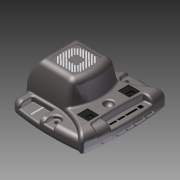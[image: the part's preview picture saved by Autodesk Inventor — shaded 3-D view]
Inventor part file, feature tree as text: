
AUTODESK INVENTOR PART (.ipt)
format: ipt  version: 2014 (Build 180170000, 170)  size: 2,946,560 bytes
history: native  units: mm
features: extrude x8, sketch x6, mirror x3, plane x2, imported_body x1, other x1
ambient origin geometry x8: Origin, YZ Plane, XZ Plane, XY Plane, X Axis, Y Axis, Z Axis, Center Point
bodies: Solid1 (feature_tree)
feature tree (21):
  imported_body  "Base1"
  sketch  "Sketch1"  dims[d50=0.9144mm d57=1.467403mm]
  extrude  "Extrusion2"  Depth=1.467403mm
  plane  "Work Plane1"
  mirror  "Mirror1"
  extrude  "Extrusion3"  Depth=1.467403mm
  sketch  "Sketch2"  dims[d58=1.467403mm d59=1.467403mm]
  extrude  "Extrusion4"  Depth=1.467403mm
  extrude  "Extrusion6"  Depth=1.467403mm
  extrude  "Extrusion7"  TaperAngle=90.0deg  [1 undecoded]
  mirror  "Mirror2"
  extrude  "Extrusion8"  Depth=1.27mm
  mirror  "Mirror3"
  sketch  "Sketch5"  dims[d62=1.467403mm d63=1.467403mm]
  other  "Work Axis1"
  extrude  "Extrusion9"  Depth=1.27mm TaperAngle=0.0deg
  plane  "Work Plane2"
  extrude  "Extrusion10"  Depth=1.27mm
  sketch  "Sketch4"  dims[d60=1.467403mm d61=1.467403mm]
  sketch  "Sketch6"  dims[d66=1.27mm d67=0.0mm d70=90.0deg]
  sketch  "Sketch7"  dims[d71=1.27mm d72=0.0mm d73=9.7282mm d75=0.762mm d76=0.0mm d77=0.762mm d80=2.54mm d81=0.0mm d82=0.254mm d83=0.0mm d84=1.016mm d85=0.0mm d86=1.27mm d87=2.286mm d88=4.572mm d89=4.572mm d90=3.81mm d91=0.0mm d92=-15.24mm d160=0.254mm d162=1.27mm d169=0.635mm d182=1.27mm d183=0.0mm]
note: 1 required parameter value undecoded (feature->parameter linkage not recoverable at this tier; creation-order binding heuristic only, values carry confidence <= 0.55)
